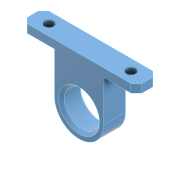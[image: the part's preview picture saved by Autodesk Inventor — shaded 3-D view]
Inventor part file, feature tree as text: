
AUTODESK INVENTOR PART (.ipt)
format: ipt  version: 2022 (Build 260153000, 153)  size: 159,232 bytes
history: native  units: mm
features: projected_geometry x3, extrude x2, chamfer x2, sketch x2, hole x1
ambient origin geometry x8: Origin, YZ Plane, XZ Plane, XY Plane, X Axis, Y Axis, Z Axis, Center Point
bodies: Solid1 (feature_tree)
feature tree (10):
  extrude  "Extrusion1"  Depth=10.0mm
  extrude  "Extrusion2"  Depth=18.0mm
  hole  "Hole1"  [1 undecoded]
  chamfer  "Chamfer2"  Distance=12.0mm
  chamfer  "Chamfer3"  Distance=3.0mm
  sketch  "Sketch3"  dims[d2=2.5mm d3=10.0mm]
  sketch  "Sketch4"  dims[d4=1.5mm d5=18.0mm d6=8.0mm d7=0.0mm d8=12.0mm d9=3.0mm d10=0.0mm d11=3.4mm d12=6.0mm d13=6.0mm d14=2.0mm d15=90.0deg d16=8.0mm d17=20.594885mm d22=1.0mm d23=2.0mm d24=45.0deg d25=2.0mm d26=2.0mm d27=45.0deg]
  projected_geometry  "Projected Loop1"
  projected_geometry  "Projected Loop2"
  projected_geometry  "Project Cut Edges1"
note: 1 required parameter value undecoded (feature->parameter linkage not recoverable at this tier; creation-order binding heuristic only, values carry confidence <= 0.55)
